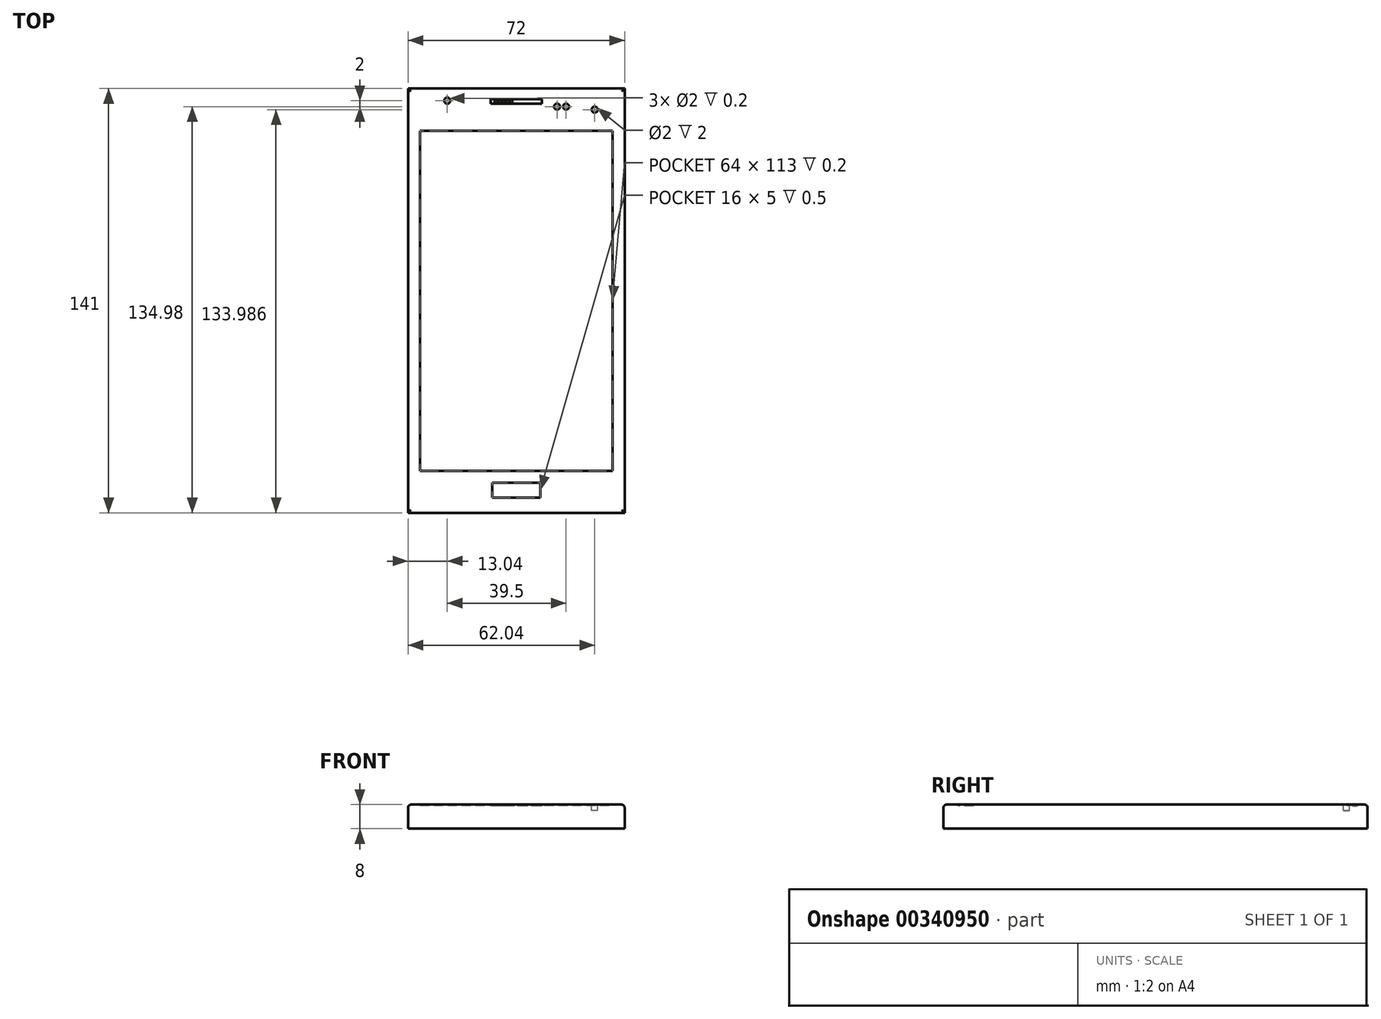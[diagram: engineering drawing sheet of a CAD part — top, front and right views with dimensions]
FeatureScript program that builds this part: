
annotation { "Feature Type Name" : "Feature", "Feature Type Description" : "" }
export const myFeature = defineFeature(function(context is Context, id is Id, definition is map)
    precondition{}
    {
        {
            var Q0;
            Q0=qCreatedBy(makeId("Top.planeOp"),FACE);
            var sketch = newSketch(context, id + "F0", { "sketchPlane" : qUnion([Q0])});
            skLineSegment(sketch, "E0.bottom", {"start": v(-36, 70.5) * mm, "end": v(36, 70.5) * mm});
            skLineSegment(sketch, "E0.top", {"start": v(-36, -70.5) * mm, "end": v(36, -70.5) * mm});
            skLineSegment(sketch, "E0.left", {"start": v(-36, 70.5) * mm, "end": v(-36, -70.5) * mm});
            skLineSegment(sketch, "E0.right", {"start": v(36, 70.5) * mm, "end": v(36, -70.5) * mm});
            skPoint(sketch, "E0.middle", {"position": v(0, 0) * mm});
            skPoint(sketch, "E1.end.orphan", {"position": v(0, 70.5) * mm});
            skPoint(sketch, "E2.end.orphan", {"position": v(0, -70.5) * mm});
            skLineSegment(sketch, "E3.bottom", {"start": v(8, -60.5) * mm, "end": v(-8, -60.5) * mm});
            skLineSegment(sketch, "E3.top", {"start": v(8, -65.5) * mm, "end": v(-8, -65.5) * mm});
            skLineSegment(sketch, "E3.left", {"start": v(8, -60.5) * mm, "end": v(8, -65.5) * mm});
            skLineSegment(sketch, "E3.right", {"start": v(-8, -60.5) * mm, "end": v(-8, -65.5) * mm});
            skPoint(sketch, "E3.middle", {"position": v(0, -63) * mm});
            skPoint(sketch, "E4.orphan", {"position": v(0, -60.5) * mm});
            skPoint(sketch, "E5.end.orphan", {"position": v(0, -65.5) * mm});
            skLineSegment(sketch, "E6", {"start": v(0, 67) * mm, "end": v(0, 66.99) * mm, "construction": true});
            skLineSegment(sketch, "E7", {"start": v(0, 65.74) * mm, "end": v(0, 66.24) * mm});
            skLineSegment(sketch, "E8.bottom", {"start": v(8.5, 65.49) * mm, "end": v(-8.5, 65.49) * mm});
            skLineSegment(sketch, "E8.top", {"start": v(8.5, 66.99) * mm, "end": v(-8.5, 66.99) * mm});
            skLineSegment(sketch, "E8.left", {"start": v(8.5, 65.49) * mm, "end": v(8.5, 66.99) * mm});
            skLineSegment(sketch, "E8.right", {"start": v(-8.5, 65.49) * mm, "end": v(-8.5, 66.99) * mm});
            skPoint(sketch, "E8.middle", {"position": v(0, 66.24) * mm});
            skCircle(sketch, "E9", {"center": v(0, 66.24) * mm, "radius": 0.5 * mm});
            skCircle(sketch, "E10", {"center": v(1.75, 66.25) * mm, "radius": 0.5 * mm});
            skCircle(sketch, "E11", {"center": v(3, 66.25) * mm, "radius": 0.5 * mm});
            skCircle(sketch, "E12", {"center": v(4.25, 66.24) * mm, "radius": 0.5 * mm});
            skCircle(sketch, "E13", {"center": v(5.5, 66.25) * mm, "radius": 0.5 * mm});
            skCircle(sketch, "E14", {"center": v(6.75, 66.25) * mm, "radius": 0.5 * mm});
            skCircle(sketch, "E15", {"center": v(7.89, 66.24) * mm, "radius": 0.5 * mm});
            skCircle(sketch, "E16.MirrorC", {"center": v(-1.75, 66.25) * mm, "radius": 0.5 * mm});
            skCircle(sketch, "E17.MirrorC", {"center": v(-4.25, 66.24) * mm, "radius": 0.5 * mm});
            skCircle(sketch, "E18.MirrorC", {"center": v(-5.5, 66.25) * mm, "radius": 0.5 * mm});
            skCircle(sketch, "E19.MirrorC", {"center": v(-6.75, 66.25) * mm, "radius": 0.5 * mm});
            skCircle(sketch, "E20.MirrorC", {"center": v(-3, 66.25) * mm, "radius": 0.5 * mm});
            skCircle(sketch, "E21", {"center": v(-7.89, 66.24) * mm, "radius": 0.5 * mm});
            skPoint(sketch, "E22.end.orphan", {"position": v(21, 63.5) * mm});
            skCircle(sketch, "E23", {"center": v(26, 63.5) * mm, "radius": 1 * mm, "construction": true});
            skPoint(sketch, "E24.end.orphan", {"position": v(27, 63.5) * mm});
            skPoint(sketch, "E24.start.orphan", {"position": v(36, 63.5) * mm});
            skPoint(sketch, "E25.end.orphan", {"position": v(12.5, 65.5) * mm});
            skPoint(sketch, "E25.start.orphan", {"position": v(16.5, 65.51) * mm});
            skPoint(sketch, "E26.orphan", {"position": v(12.5, 70.5) * mm});
            skCircle(sketch, "E27", {"center": v(13.5, 64.5) * mm, "radius": 1 * mm});
            skCircle(sketch, "E28", {"center": v(16.5, 64.5) * mm, "radius": 1 * mm});
            skPoint(sketch, "E29.end.orphan", {"position": v(12.5, 64.5) * mm});
            skPoint(sketch, "E30.start.orphan", {"position": v(14.5, 64.5) * mm});
            skPoint(sketch, "E31.end.orphan", {"position": v(17.5, 64.5) * mm});
            skLineSegment(sketch, "E32", {"start": v(32, 56.5) * mm, "end": v(32, -56.5) * mm});
            skLineSegment(sketch, "E33", {"start": v(32, -56.5) * mm, "end": v(-32, -56.5) * mm});
            skLineSegment(sketch, "E34", {"start": v(-32, -56.5) * mm, "end": v(-32, 56.5) * mm});
            skLineSegment(sketch, "E35", {"start": v(-32, 56.5) * mm, "end": v(32, 56.5) * mm});
            skPoint(sketch, "E36.orphan", {"position": v(-0.5, 66.25) * mm});
            skPoint(sketch, "E37.orphan", {"position": v(8.5, 66.24) * mm});
            skPoint(sketch, "E38.orphan", {"position": v(0.5, 66.25) * mm});
            skPoint(sketch, "E39.trimOffspring.end.orphan", {"position": v(4.25, 66.25) * mm});
            skPoint(sketch, "E40.orphan", {"position": v(-8.5, 66.24) * mm});
            skPoint(sketch, "E41.orphan", {"position": v(-4.25, 66.25) * mm});
            skPoint(sketch, "E42.start.orphan", {"position": v(15.5, 64.5) * mm});
            skPoint(sketch, "E43.end.orphan", {"position": v(25, 63.5) * mm});
            skPoint(sketch, "E44.end.orphan", {"position": v(-29.3, 64.5) * mm});
            skPoint(sketch, "E44.start.orphan", {"position": v(-30.38, 66.5) * mm});
            skCircle(sketch, "E45", {"center": v(-23, 66.5) * mm, "radius": 1 * mm});
            skPoint(sketch, "E46.orphan", {"position": v(-36, 66.5) * mm});
            skPoint(sketch, "E47.orphan", {"position": v(-23, 64.5) * mm});
            skCircle(sketch, "E48", {"center": v(26, 63.5) * mm, "radius": 1 * mm});
            skSolve(sketch);
        }
        {
            var Q0;
            Q0=makeQuery(id+"F0.imprint","IMPRINT",FACE,{"disambiguationData":[TD([[makeQuery(id+"F0.imprint","IMPRINT",EDGE,{"derivedFrom":sQuery(id+"F0.wireOp",EDGE,"E0.bottom")}),-1.0]])]});
            var sketch = newSketch(context, id + "F1", { "sketchPlane" : qUnion([Q0])});
            skLineSegment(sketch, "E49", {"start": v(35.96, 70.52) * mm, "end": v(35.96, -70.48) * mm});
            skLineSegment(sketch, "E50", {"start": v(35.96, -70.48) * mm, "end": v(-36.04, -70.48) * mm});
            skLineSegment(sketch, "E51", {"start": v(-36.04, -70.48) * mm, "end": v(-36.04, 70.52) * mm});
            skLineSegment(sketch, "E52", {"start": v(-36.04, 70.52) * mm, "end": v(35.96, 70.52) * mm});
            skSolve(sketch);
        }
        {
            var Q0;
            Q0 = qSketchRegion(id + "F1", true);
            extrude(context, id + "F2", {"entities" : qUnion([Q0]), "oppositeDirection" : true, "depth" : 8 * mm});
        }
        {
            var Q0;
            Q0=makeQuery(id+"F0.imprint","IMPRINT",FACE,{"disambiguationData":[TD([[makeQuery(id+"F0.imprint","IMPRINT",EDGE,{"derivedFrom":sQuery(id+"F0.wireOp",EDGE,"E45")}),1.0]])]});
            var Q1;
            Q1=makeQuery(id+"F0.imprint","IMPRINT",FACE,{"disambiguationData":[TD([[makeQuery(id+"F0.imprint","IMPRINT",EDGE,{"derivedFrom":sQuery(id+"F0.wireOp",EDGE,"E27")}),1.0]])]});
            var Q2;
            Q2=makeQuery(id+"F0.imprint","IMPRINT",FACE,{"disambiguationData":[TD([[makeQuery(id+"F0.imprint","IMPRINT",EDGE,{"derivedFrom":sQuery(id+"F0.wireOp",EDGE,"E28")}),1.0]])]});
            extrude(context, id + "F3", {"entities" : qUnion([Q0, Q1, Q2]), "operationType" : NewBodyOperationType.REMOVE, "oppositeDirection" : true, "depth" : .2 * mm});
        }
        {
            var Q0;
            Q0=makeQuery(id+"F0.imprint","IMPRINT",FACE,{"disambiguationData":[TD([[makeQuery(id+"F0.imprint","IMPRINT",EDGE,{"derivedFrom":sQuery(id+"F0.wireOp",EDGE,"E32")}),-1.0]])]});
            var Q1;
            Q1=makeQuery(id+"F0.imprint","IMPRINT",FACE,{"disambiguationData":[TD([[makeQuery(id+"F0.imprint","IMPRINT",EDGE,{"derivedFrom":sQuery(id+"F0.wireOp",EDGE,"E8.bottom")}),-1.0]])]});
            extrude(context, id + "F4", {"entities" : qUnion([Q0, Q1]), "operationType" : NewBodyOperationType.REMOVE, "oppositeDirection" : true, "depth" : .2 * mm});
        }
        {
            var Q0;
            Q0=makeQuery(id+"F0.imprint","IMPRINT",FACE,{"disambiguationData":[TD([[makeQuery(id+"F0.imprint","IMPRINT",EDGE,{"derivedFrom":sQuery(id+"F0.wireOp",EDGE,"E21")}),1.0]])]});
            var Q1;
            Q1=makeQuery(id+"F0.imprint","IMPRINT",FACE,{"disambiguationData":[TD([[makeQuery(id+"F0.imprint","IMPRINT",EDGE,{"derivedFrom":sQuery(id+"F0.wireOp",EDGE,"E19.MirrorC")}),-1.0]])]});
            var Q2;
            Q2=makeQuery(id+"F0.imprint","IMPRINT",FACE,{"disambiguationData":[TD([[makeQuery(id+"F0.imprint","IMPRINT",EDGE,{"derivedFrom":sQuery(id+"F0.wireOp",EDGE,"E10")}),1.0]])]});
            var Q3;
            Q3=makeQuery(id+"F0.imprint","IMPRINT",FACE,{"disambiguationData":[TD([[makeQuery(id+"F0.imprint","IMPRINT",EDGE,{"derivedFrom":sQuery(id+"F0.wireOp",EDGE,"E11")}),1.0]])]});
            var Q4;
            Q4=makeQuery(id+"F0.imprint","IMPRINT",FACE,{"disambiguationData":[TD([[makeQuery(id+"F0.imprint","IMPRINT",EDGE,{"derivedFrom":sQuery(id+"F0.wireOp",EDGE,"E9")}),1.0]])]});
            var Q5;
            Q5=makeQuery(id+"F0.imprint","IMPRINT",FACE,{"disambiguationData":[TD([[makeQuery(id+"F0.imprint","IMPRINT",EDGE,{"derivedFrom":sQuery(id+"F0.wireOp",EDGE,"E17.MirrorC")}),-1.0]])]});
            var Q6;
            Q6=makeQuery(id+"F0.imprint","IMPRINT",FACE,{"disambiguationData":[TD([[makeQuery(id+"F0.imprint","IMPRINT",EDGE,{"derivedFrom":sQuery(id+"F0.wireOp",EDGE,"E20.MirrorC")}),-1.0]])]});
            var Q7;
            Q7=makeQuery(id+"F0.imprint","IMPRINT",FACE,{"disambiguationData":[TD([[makeQuery(id+"F0.imprint","IMPRINT",EDGE,{"derivedFrom":sQuery(id+"F0.wireOp",EDGE,"E16.MirrorC")}),-1.0]])]});
            var Q8;
            Q8=makeQuery(id+"F0.imprint","IMPRINT",FACE,{"disambiguationData":[TD([[makeQuery(id+"F0.imprint","IMPRINT",EDGE,{"derivedFrom":sQuery(id+"F0.wireOp",EDGE,"E12")}),1.0]])]});
            var Q9;
            Q9=makeQuery(id+"F0.imprint","IMPRINT",FACE,{"disambiguationData":[TD([[makeQuery(id+"F0.imprint","IMPRINT",EDGE,{"derivedFrom":sQuery(id+"F0.wireOp",EDGE,"E13")}),1.0]])]});
            var Q10;
            Q10=makeQuery(id+"F0.imprint","IMPRINT",FACE,{"disambiguationData":[TD([[makeQuery(id+"F0.imprint","IMPRINT",EDGE,{"derivedFrom":sQuery(id+"F0.wireOp",EDGE,"E14")}),1.0]])]});
            var Q11;
            Q11=makeQuery(id+"F0.imprint","IMPRINT",FACE,{"disambiguationData":[TD([[makeQuery(id+"F0.imprint","IMPRINT",EDGE,{"derivedFrom":sQuery(id+"F0.wireOp",EDGE,"E15")}),1.0]])]});
            var Q12;
            Q12=makeQuery(id+"F0.imprint","IMPRINT",FACE,{"disambiguationData":[TD([[makeQuery(id+"F0.imprint","IMPRINT",EDGE,{"derivedFrom":sQuery(id+"F0.wireOp",EDGE,"E18.MirrorC")}),-1.0]])]});
            extrude(context, id + "F5", {"entities" : qUnion([Q0, Q1, Q2, Q3, Q4, Q5, Q6, Q7, Q8, Q9, Q10, Q11, Q12]), "operationType" : NewBodyOperationType.REMOVE, "oppositeDirection" : true, "depth" : .5 * mm});
        }
        {
            var Q0;
            Q0=makeQuery(id+"F1.imprint","IMPRINT",FACE,{"disambiguationData":[TD([[makeQuery(id+"F1.imprint","IMPRINT",EDGE,{"derivedFrom":makeQuery(id+"F0.imprint","IMPRINT",EDGE,{"derivedFrom":sQuery(id+"F0.wireOp",EDGE,"E48")})}),1.0]])]});
            extrude(context, id + "F6", {"entities" : qUnion([Q0]), "operationType" : NewBodyOperationType.REMOVE, "oppositeDirection" : true, "depth" : 2 * mm});
        }
        {
            var Q0;
            Q0=makeQuery(id+"F0.imprint","IMPRINT",FACE,{"disambiguationData":[TD([[makeQuery(id+"F0.imprint","IMPRINT",EDGE,{"derivedFrom":sQuery(id+"F0.wireOp",EDGE,"E3.bottom")}),1.0]])]});
            extrude(context, id + "F7", {"entities" : qUnion([Q0]), "operationType" : NewBodyOperationType.REMOVE, "oppositeDirection" : true, "depth" : .5 * mm});
        }
        {
            var Q0;
            Q0=makeQuery(id+"F2.opExtrude","CAP_EDGE",EDGE,{"disambiguationData":[OSD([sQuery(id+"F1.wireOp",EDGE,"E52")])],"isStart":true});
            var Q1;
            Q1=makeQuery(id+"F2.opExtrude","CAP_EDGE",EDGE,{"disambiguationData":[OSD([sQuery(id+"F1.wireOp",EDGE,"E51")])],"isStart":true});
            var Q2;
            Q2=makeQuery(id+"F2.opExtrude","CAP_EDGE",EDGE,{"disambiguationData":[OSD([sQuery(id+"F1.wireOp",EDGE,"E49")])],"isStart":true});
            var Q3;
            Q3=makeQuery(id+"F2.opExtrude","CAP_EDGE",EDGE,{"disambiguationData":[OSD([sQuery(id+"F1.wireOp",EDGE,"E50")])],"isStart":true});
            var Q4;
            Q4=makeQuery(id+"F7.boolean.opBoolean","COPY",EDGE,{"derivedFrom":makeQuery(id+"F7.opExtrude","CAP_EDGE",EDGE,{"disambiguationData":[OSD([sQuery(id+"F0.wireOp",EDGE,"E3.bottom")])],"isStart":true})});
            var Q5;
            Q5=makeQuery(id+"F7.boolean.opBoolean","COPY",EDGE,{"derivedFrom":makeQuery(id+"F7.opExtrude","CAP_EDGE",EDGE,{"disambiguationData":[OSD([sQuery(id+"F0.wireOp",EDGE,"E3.right")])],"isStart":true})});
            var Q6;
            Q6=makeQuery(id+"F7.boolean.opBoolean","COPY",EDGE,{"derivedFrom":makeQuery(id+"F7.opExtrude","CAP_EDGE",EDGE,{"disambiguationData":[OSD([sQuery(id+"F0.wireOp",EDGE,"E3.left")])],"isStart":true})});
            var Q7;
            Q7=makeQuery(id+"F7.boolean.opBoolean","COPY",EDGE,{"derivedFrom":makeQuery(id+"F7.opExtrude","CAP_EDGE",EDGE,{"disambiguationData":[OSD([sQuery(id+"F0.wireOp",EDGE,"E3.top")])],"isStart":true})});
            fillet(context, id + "F8", {"entities" : qUnion([Q0, Q1, Q2, Q3, Q4, Q5, Q6, Q7]), "radius" : 1 * mm, "tangentPropagation" : true, "allowEdgeOverflow" : false});
        }
    });
